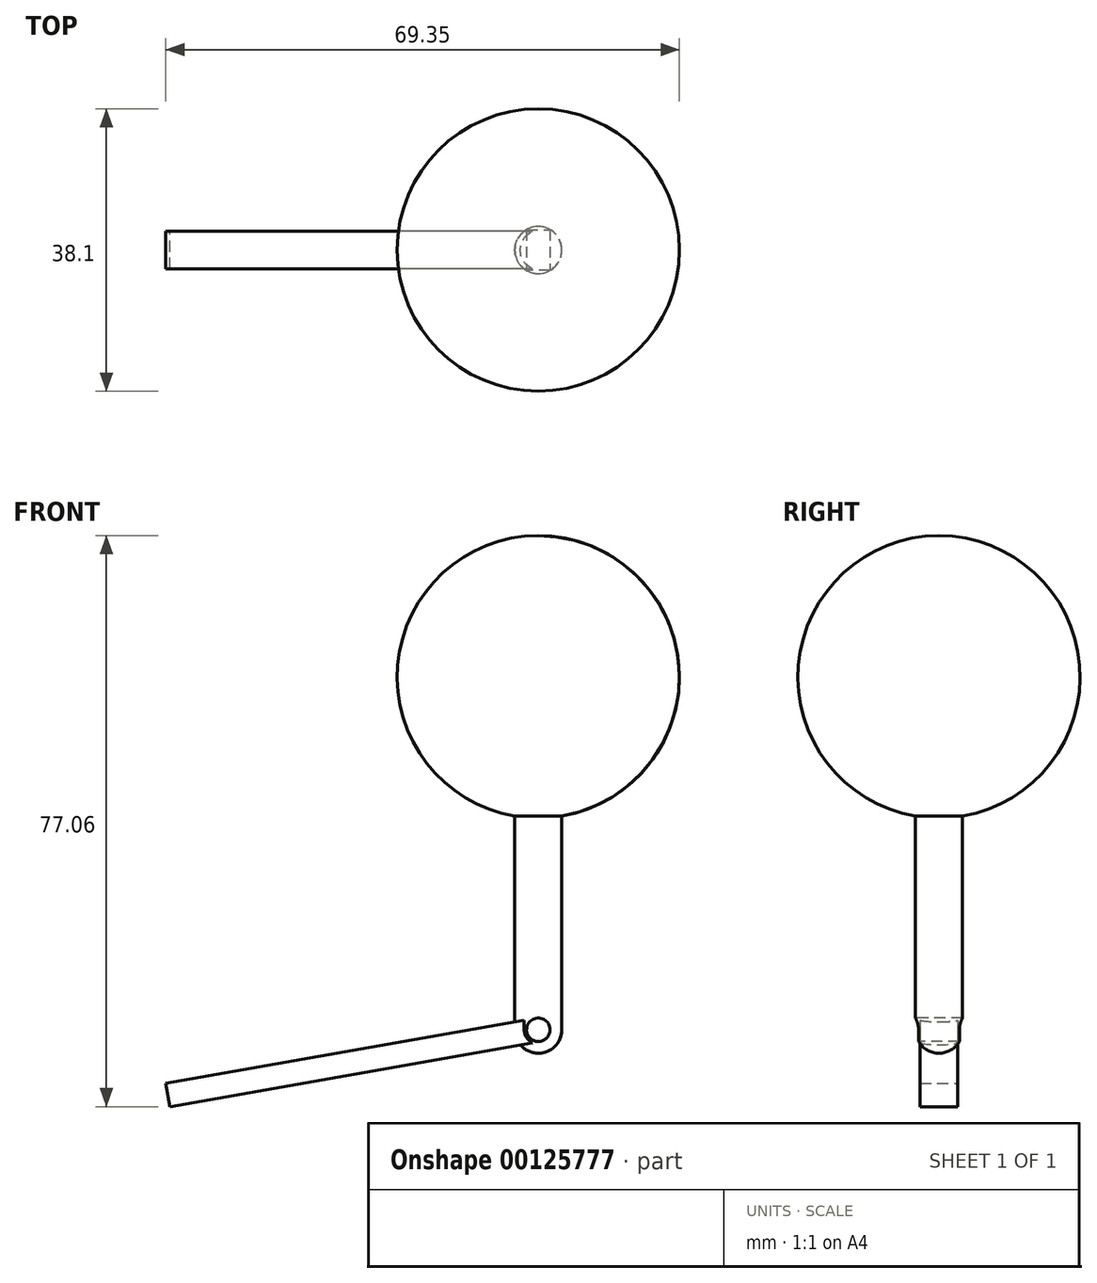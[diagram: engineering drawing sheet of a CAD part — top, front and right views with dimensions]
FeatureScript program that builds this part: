
annotation { "Feature Type Name" : "Feature", "Feature Type Description" : "" }
export const myFeature = defineFeature(function(context is Context, id is Id, definition is map)
    precondition{}
    {
        {
            var Q0;
            Q0=qCreatedBy(makeId("Front.planeOp"),FACE);
            var sketch = newSketch(context, id + "F0", { "sketchPlane" : qUnion([Q0])});
            skLineSegment(sketch, "E0", {"start": v(0, 0) * mm, "end": v(0, -50.8) * mm});
            skArc(sketch, "E1", {"start": v(3.18, -18.78) * mm, "mid": v(18.98, 1.6) * mm, "end": v(0, 19.05) * mm});
            skLineSegment(sketch, "E2", {"start": v(0, 0) * mm, "end": v(0, 19.05) * mm});
            skLineSegment(sketch, "E3", {"start": v(3.17, -18.78) * mm, "end": v(3.18, -47.62) * mm});
            skArc(sketch, "E4", {"start": v(3.18, -47.62) * mm, "mid": v(2.25, -49.87) * mm, "end": v(0, -50.8) * mm});
            skLineSegment(sketch, "E5", {"start": v(0, 19.05) * mm, "end": v(0, 64.27) * mm, "construction": true});
            skSolve(sketch);
        }
        {
            var Q0;
            Q0=qSketchRegion(id+"F0",true);
            var Q1;
            Q1=sQuery(id+"F0.wireOp",EDGE,"E5");
            revolve(context, id + "F1", {"entities" : qUnion([Q0]), "axis" : qUnion([Q1]), "revolveType" : RevolveType.FULL});
        }
        {
            var Q0;
            Q0=qCreatedBy(makeId("Front.planeOp"),FACE);
            var sketch = newSketch(context, id + "F2", { "sketchPlane" : qUnion([Q0])});
            skCircle(sketch, "E6", {"center": v(0, -47.62) * mm, "radius": 1.59 * mm});
            skSolve(sketch);
        }
        {
            var Q0;
            Q0=qSketchRegion(id+"F2",true);
            extrude(context, id + "F3", {"entities" : qUnion([Q0]), "operationType" : NewBodyOperationType.REMOVE, "endBound" : BoundingType.SYMMETRIC, "oppositeDirection" : true, "depth" : 25.4 * mm});
        }
        {
            var Q0;
            Q0=qCreatedBy(makeId("Front.planeOp"),FACE);
            var sketch = newSketch(context, id + "F4", { "sketchPlane" : qUnion([Q0])});
            skPoint(sketch, "E7", {"position": v(0, -47.62) * mm});
            skLineSegment(sketch, "E8", {"start": v(0, -47.62) * mm, "end": v(0, -21.02) * mm, "construction": true});
            skLineSegment(sketch, "E9", {"start": v(0, -47.62) * mm, "end": v(-50.03, -56.45) * mm, "construction": true});
            skArc(sketch, "E10.0", {"start": v(1.59, -47.62) * mm, "mid": v(0, -46.04) * mm, "end": v(-1.59, -47.62) * mm});
            skArc(sketch, "E11.0", {"start": v(1.59, -47.62) * mm, "mid": v(0, -49.21) * mm, "end": v(-1.59, -47.62) * mm});
            skLineSegment(sketch, "E12", {"start": v(-0.28, -46.06) * mm, "end": v(-50.3, -54.88) * mm});
            skPoint(sketch, "E13.endSnap0", {"position": v(0, -49.21) * mm});
            skLineSegment(sketch, "E14", {"start": v(-0.28, -46.06) * mm, "end": v(0.28, -49.19) * mm});
            skLineSegment(sketch, "E15", {"start": v(0.28, -49.19) * mm, "end": v(-49.75, -58) * mm});
            skLineSegment(sketch, "E16", {"start": v(-50.3, -54.88) * mm, "end": v(-49.75, -58) * mm});
            skArc(sketch, "E17", {"start": v(0.28, -49.19) * mm, "mid": v(1.62, -47.34) * mm, "end": v(-0.28, -46.06) * mm});
            skLineSegment(sketch, "E18", {"start": v(-25.29, -50.47) * mm, "end": v(-24.74, -53.6) * mm, "construction": true});
            skArc(sketch, "E19.MirrorCS", {"start": v(-49.75, -58) * mm, "mid": v(-51.64, -56.73) * mm, "end": v(-50.3, -54.88) * mm});
            skSolve(sketch);
        }
        {
            var Q0;
            {var subQ6=sQuery(id+"F4.wireOp",EDGE,"E12");Q0=makeQuery(id+"F4.imprint","IMPRINT",FACE,{"disambiguationData":[TD([[makeQuery(id+"F4.imprint","IMPRINT",EDGE,{"derivedFrom":subQ6}),1.0]])]});}
            extrude(context, id + "F5", {"entities" : qUnion([Q0]), "operationType" : NewBodyOperationType.ADD, "endBound" : BoundingType.SYMMETRIC, "depth" : 5.08 * mm});
        }
    });
